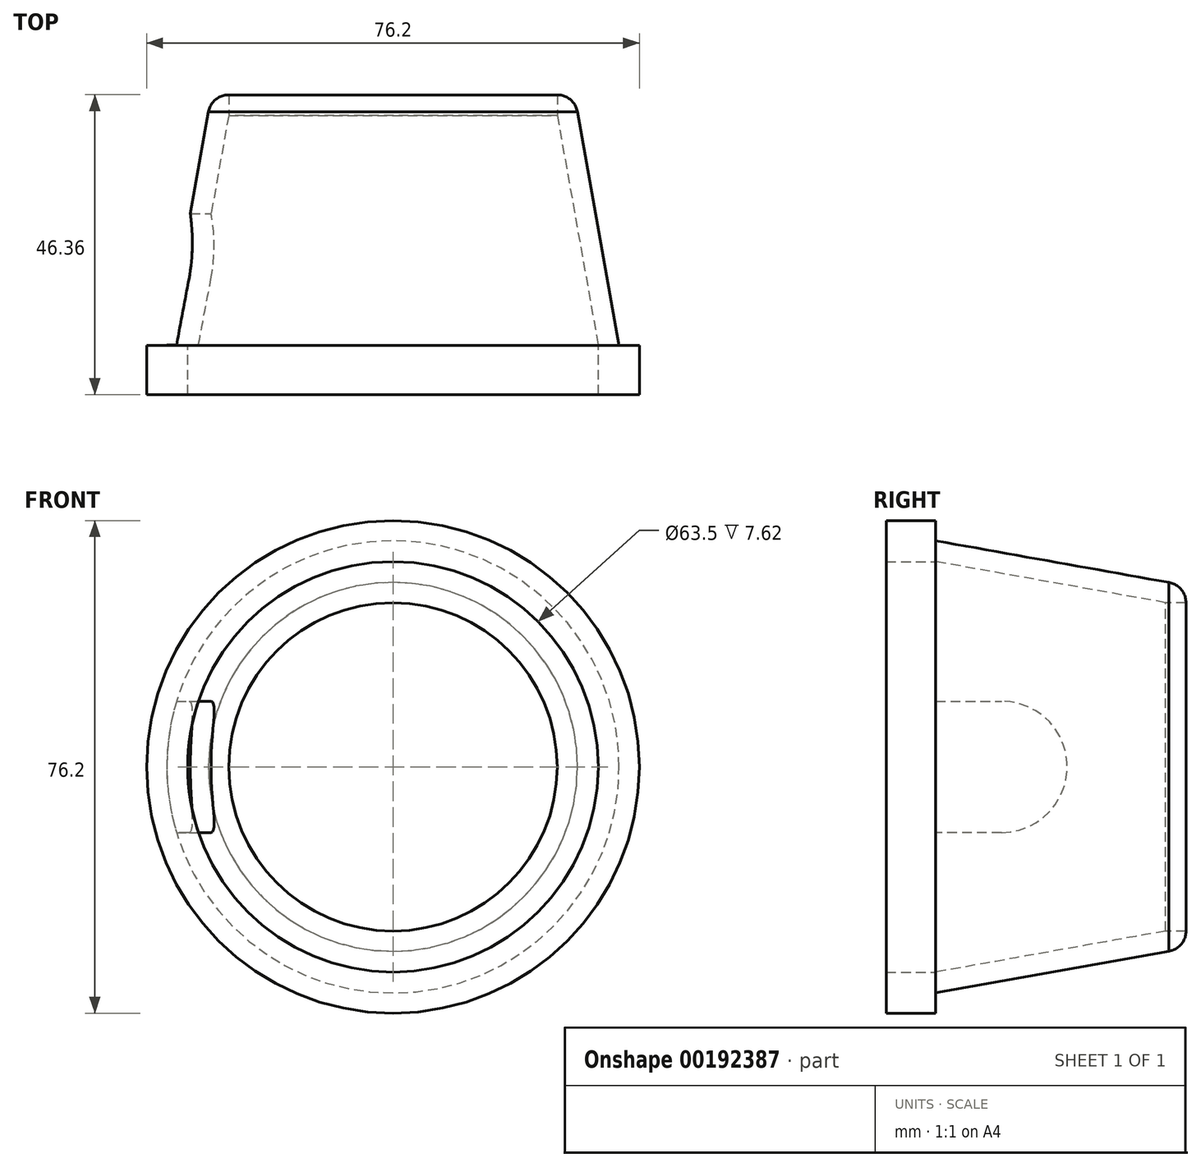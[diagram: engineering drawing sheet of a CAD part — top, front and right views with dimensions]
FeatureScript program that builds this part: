
annotation { "Feature Type Name" : "Feature", "Feature Type Description" : "" }
export const myFeature = defineFeature(function(context is Context, id is Id, definition is map)
    precondition{}
    {
        {
            var Q0;
            Q0=qCreatedBy(makeId("Right.planeOp"),FACE);
            var sketch = newSketch(context, id + "F0", { "sketchPlane" : qUnion([Q0])});
            skLineSegment(sketch, "E0", {"start": v(0, 0) * mm, "end": v(-35.56, 0) * mm});
            skLineSegment(sketch, "E1", {"start": v(0, 25.4) * mm, "end": v(0, 0) * mm});
            skLineSegment(sketch, "E2", {"start": v(-35.56, 31.75) * mm, "end": v(-35.56, 0) * mm});
            skLineSegment(sketch, "E3", {"start": v(-35.56, 31.75) * mm, "end": v(0, 25.4) * mm});
            skLineSegment(sketch, "E4.1", {"start": v(-35.56, 34.98) * mm, "end": v(0.54, 28.53) * mm});
            skLineSegment(sketch, "E5", {"start": v(-35.56, 31.75) * mm, "end": v(-35.56, 34.98) * mm});
            skLineSegment(sketch, "E6", {"start": v(0.54, 28.53) * mm, "end": v(0, 25.4) * mm});
            skLineSegment(sketch, "E7", {"start": v(-43.18, 0) * mm, "end": v(-43.18, 38.1) * mm});
            skLineSegment(sketch, "E8", {"start": v(-43.18, 38.1) * mm, "end": v(-35.56, 38.1) * mm});
            skLineSegment(sketch, "E9", {"start": v(-35.56, 38.1) * mm, "end": v(-35.56, 0) * mm});
            skLineSegment(sketch, "E10", {"start": v(-35.56, 0) * mm, "end": v(-43.18, 0) * mm});
            skLineSegment(sketch, "E11", {"start": v(-35.56, 31.75) * mm, "end": v(-43.18, 31.75) * mm});
            skSolve(sketch);
        }
        {
            var Q0;
            Q0=qCreatedBy(makeId("Top.planeOp"),FACE);
            var sketch = newSketch(context, id + "F1", { "sketchPlane" : qUnion([Q0])});
            skLineSegment(sketch, "E12", {"start": v(-25.4, 0) * mm, "end": v(-28.58, 0) * mm});
            skLineSegment(sketch, "E13", {"start": v(-28.58, 0) * mm, "end": v(0, 0) * mm});
            skLineSegment(sketch, "E14", {"start": v(0, 0) * mm, "end": v(-25.4, 0) * mm});
            skLineSegment(sketch, "E15", {"start": v(25.4, 0) * mm, "end": v(0, 0) * mm});
            skLineSegment(sketch, "E16", {"start": v(25.4, 0) * mm, "end": v(28.58, 0) * mm});
            skLineSegment(sketch, "E17", {"start": v(-28.58, 0) * mm, "end": v(-25.4, 0) * mm});
            skArc(sketch, "E18", {"start": v(-28.58, 0) * mm, "mid": v(-27.72, 2.17) * mm, "end": v(-25.62, 3.17) * mm});
            skArc(sketch, "E19", {"start": v(25.4, 3.17) * mm, "mid": v(27.65, 2.25) * mm, "end": v(28.58, 0) * mm});
            skLineSegment(sketch, "E20", {"start": v(0, -35.76) * mm, "end": v(-34.93, -35.76) * mm});
            skLineSegment(sketch, "E21", {"start": v(0, -35.76) * mm, "end": v(34.93, -35.76) * mm});
            skLineSegment(sketch, "E22", {"start": v(-34.93, -35.76) * mm, "end": v(-31.75, -35.76) * mm});
            skLineSegment(sketch, "E23", {"start": v(34.93, -35.76) * mm, "end": v(31.75, -35.76) * mm});
            skLineSegment(sketch, "E24", {"start": v(-34.93, -35.76) * mm, "end": v(-28.58, 0) * mm});
            skLineSegment(sketch, "E25", {"start": v(-31.75, -35.76) * mm, "end": v(-25.4, 0) * mm});
            skLineSegment(sketch, "E26", {"start": v(25.4, 0) * mm, "end": v(31.75, -35.76) * mm});
            skLineSegment(sketch, "E27", {"start": v(28.57, 0) * mm, "end": v(34.92, -35.76) * mm});
            skLineSegment(sketch, "E28", {"start": v(-25.4, 0) * mm, "end": v(-25.4, 3.17) * mm});
            skLineSegment(sketch, "E29", {"start": v(25.4, 0) * mm, "end": v(25.4, 3.17) * mm});
            skLineSegment(sketch, "E30", {"start": v(25.4, 3.17) * mm, "end": v(-25.4, 3.17) * mm});
            skLineSegment(sketch, "E31", {"start": v(0, 0) * mm, "end": v(0, 3.17) * mm});
            skSolve(sketch);
        }
        {
            var Q0;
            Q0=makeQuery(id+"F0.imprint","IMPRINT",FACE,{"disambiguationData":[TD([[makeQuery(id+"F0.imprint","IMPRINT",EDGE,{"derivedFrom":sQuery(id+"F0.wireOp",EDGE,"E3")}),1.0]])]});
            var Q1;
            Q1=sQuery(id+"F0.wireOp",EDGE,"E4.1");
            var Q2;
            Q2=sQuery(id+"F0.wireOp",EDGE,"E3");
            var Q3;
            Q3=sQuery(id+"F0.wireOp",EDGE,"E0");
            revolve(context, id + "F2", {"entities" : qUnion([Q0]), "surfaceEntities" : qUnion([Q1, Q2]), "axis" : qUnion([Q3]), "revolveType" : RevolveType.TWO_DIRECTIONS, "angle" : 0 * degree, "angleBack" : 360 * degree});
        }
        {
            var Q0;
            Q0=makeQuery(id+"F1.imprint","IMPRINT",FACE,{"disambiguationData":[TD([[makeQuery(id+"F1.imprint","IMPRINT",EDGE,{"derivedFrom":sQuery(id+"F1.wireOp",EDGE,"E16")}),1.0]])]});
            var Q1;
            Q1=sQuery(id+"F1.wireOp",EDGE,"E31");
            revolve(context, id + "F3", {"operationType" : NewBodyOperationType.ADD, "entities" : qUnion([Q0]), "axis" : qUnion([Q1]), "revolveType" : RevolveType.TWO_DIRECTIONS, "angle" : 0 * degree, "angleBack" : 360 * degree});
        }
        {
            var Q0;
            {var subQ2=sQuery(id+"F0.wireOp",EDGE,"E8");Q0=makeQuery(id+"F0.imprint","IMPRINT",FACE,{"disambiguationData":[TD([[makeQuery(id+"F0.imprint","IMPRINT",EDGE,{"derivedFrom":subQ2}),-1.0]])]});}
            var Q1;
            Q1=sQuery(id+"F0.wireOp",EDGE,"E10");
            revolve(context, id + "F4", {"operationType" : NewBodyOperationType.ADD, "entities" : qUnion([Q0]), "axis" : qUnion([Q1]), "revolveType" : RevolveType.FULL});
        }
        {
            var Q0;
            Q0=qCreatedBy(makeId("Right.planeOp"),FACE);
            var sketch = newSketch(context, id + "F5", { "sketchPlane" : qUnion([Q0])});
            skLineSegment(sketch, "E32", {"start": v(-35.5, 0) * mm, "end": v(-35.5, -10.16) * mm});
            skLineSegment(sketch, "E33", {"start": v(-35.5, 0) * mm, "end": v(-35.5, 10.16) * mm});
            skLineSegment(sketch, "E34", {"start": v(-35.5, 10.16) * mm, "end": v(-35.5, 0) * mm});
            skLineSegment(sketch, "E35", {"start": v(-35.5, 10.16) * mm, "end": v(-25.35, 10.16) * mm});
            skLineSegment(sketch, "E36", {"start": v(-15.19, 0) * mm, "end": v(-15.19, 0) * mm});
            skLineSegment(sketch, "E37", {"start": v(-25.35, -10.16) * mm, "end": v(-35.5, -10.16) * mm});
            skPoint(sketch, "E38.visualSharp", {"position": v(-15.19, 10.16) * mm});
            skArc(sketch, "E38.filletArc", {"start": v(-15.19, 0) * mm, "mid": v(-18.16, 7.18) * mm, "end": v(-25.35, 10.16) * mm});
            skPoint(sketch, "E39.visualSharp", {"position": v(-15.19, -10.16) * mm});
            skArc(sketch, "E39.filletArc", {"start": v(-25.35, -10.16) * mm, "mid": v(-18.16, -7.18) * mm, "end": v(-15.19, 0) * mm});
            skSolve(sketch);
        }
        {
            var Q0;
            Q0 = qSketchRegion(id + "F5", true);
            extrude(context, id + "F6", {"entities" : qUnion([Q0]), "operationType" : NewBodyOperationType.REMOVE, "oppositeDirection" : true, "depth" : 38.1 * mm});
        }
    });
